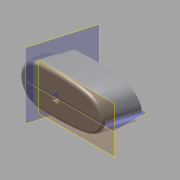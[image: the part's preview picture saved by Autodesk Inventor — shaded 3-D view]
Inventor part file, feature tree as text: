
AUTODESK INVENTOR PART (.ipt)
format: ipt  version: 2012 SP2 (Build 160219200, 219)  size: 687,616 bytes
history: native  units: in
note: dims shown in document units (in); Inventor stores cm internally (conversion verified against a paired STEP export)
features: sketch x14, sweep x5, plane x4, fillet x3, extrude x2, other x2, mirror x1, chamfer x1, projected_geometry x1, surface_op x1
ambient origin geometry x8: Origin, YZ Plane, XZ Plane, XY Plane, X Axis, Y Axis, Z Axis, Center Point
bodies: Solid1 (feature_tree)
feature tree (34):
  sketch  "Sketch1"  dims[d6=0.9405in d9=0.688in]
  plane  "Work Plane1"
  plane  "Work Plane2"
  sketch  "Sketch3"  dims[d12=0.2381in d13=0.5734in]
  plane  "Work Plane3"
  sweep  "Sweep1"
  sweep  "Sweep2"
  extrude  "Extrusion1"  Depth=0.5734in
  plane  "Work Plane4"
  mirror  "Mirror1"
  sweep  "Sweep3"
  sweep  "Sweep5"
  sweep  "Sweep6"
  fillet  "Fillet1"  Radius=0.3395in
  chamfer  "Chamfer1"  Distance=0.9887in
  extrude  "Extrusion3"  Depth=0.2944in
  fillet  "Fillet2"  Radius=1.1563in
  fillet  "Fillet3"  Radius=0.2583in
  other  "Image1"
  sketch  "Sketch2"  dims[d10=0.069in d11=0.12in]
  other  "Srf1"
  sketch  "Sketch4"  dims[d14=0.4256in d15=1.588in]
  sketch  "Sketch5"  dims[d16=0.3503in d17=0.5806in]
  sketch  "Sketch6"  dims[d18=0.3426in d19=0.2058in d20=0.3395in]
  sketch  "Sketch7"  dims[d21=0.7769in]
  sketch  "Sketch8"  dims[d22=0.3374in]
  sketch  "Sketch9"  dims[d23=0.1206in]
  sketch  "Sketch10"  dims[d24=0.3329in]
  sketch  "Sketch14"  dims[d25=0.8673in]
  sketch  "Sketch15"  dims[d26=0.3313in]
  sketch  "Sketch16"  dims[d27=0.0621in]
  sketch  "Sketch18"  dims[d28=0.323in d29=0.9887in d30=0.2944in d31=1.1563in d32=0.2583in d33=1.2792in d34=0.1988in d35=1.391in d36=0.1269in d37=1.4752in d38=0.0171in d39=1.5524in d40=0.0519in d41=1.5805in d42=0.1042in d43=1.7561in d44=0.2965in d47=0.5902in d48=0.2in d49=0.0in d50=0.6495in d51=1.035in d52=0.5105in d53=0.306in d54=0.5955in d55=0.0in d56=0.6605in d57=0.053in d58=0.1095in d59=0.2in d60=0.055in d61=0.0in d62=0.7687in d64=0.3167in d65=0.4475in d66=0.0in d67=0.0285in d68=0.0285in d69=0.0285in d70=0.0285in d71=0.0285in d72=0.0285in d76=0.0in d77=0.0in d78=0.5in d79=0.08in d80=0.0285in d81=15.0deg d85=1.0in d86=0.0in d87=0.075in d88=0.075in]
  projected_geometry  "Projected Loop2"
  surface_op  "Boundary Patch1"
